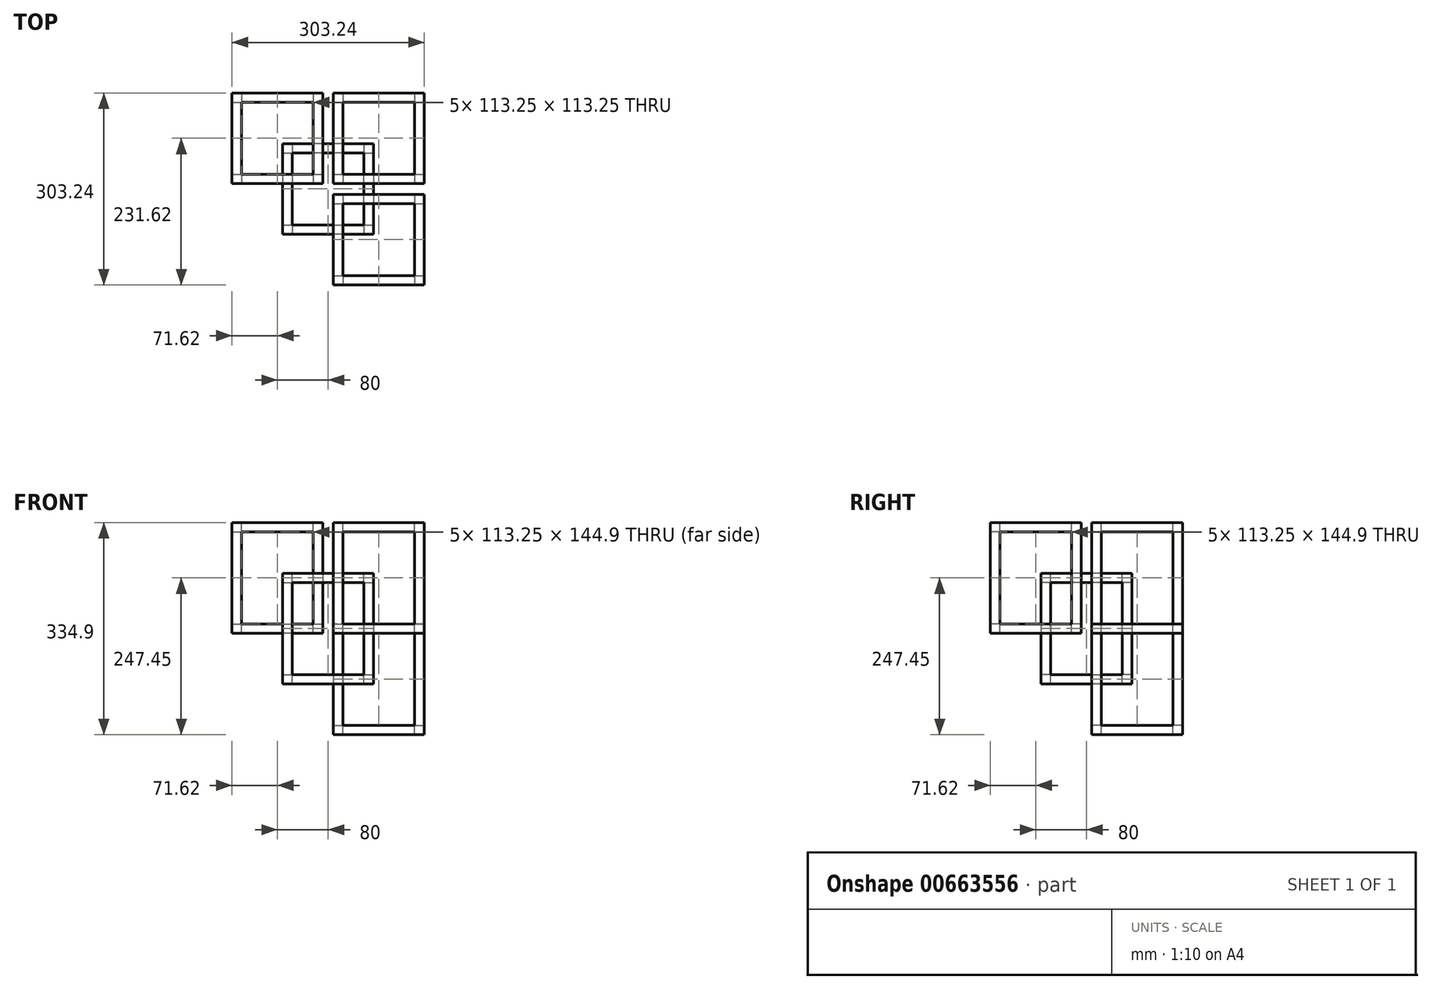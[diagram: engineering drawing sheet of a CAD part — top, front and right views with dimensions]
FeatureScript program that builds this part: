
annotation { "Feature Type Name" : "Feature", "Feature Type Description" : "" }
export const myFeature = defineFeature(function(context is Context, id is Id, definition is map)
    precondition{}
    {
        {
            var Q0;
            Q0=qCreatedBy(makeId("Top.planeOp"),FACE);
            var sketch = newSketch(context, id + "F0", { "sketchPlane" : qUnion([Q0])});
            skLineSegment(sketch, "E0.bottom", {"start": v(71.63, 71.63) * mm, "end": v(-71.62, 71.63) * mm});
            skLineSegment(sketch, "E0.top", {"start": v(71.63, -71.63) * mm, "end": v(-71.62, -71.63) * mm});
            skLineSegment(sketch, "E0.left", {"start": v(71.63, 71.62) * mm, "end": v(71.63, -71.63) * mm});
            skLineSegment(sketch, "E0.right", {"start": v(-71.62, 71.63) * mm, "end": v(-71.62, -71.63) * mm});
            skPoint(sketch, "E0.middle", {"position": v(0, 0) * mm});
            skSolve(sketch);
        }
        {
            var Q0;
            Q0=makeQuery(id+"F0.imprint","IMPRINT",FACE,{"disambiguationData":[TD([[makeQuery(id+"F0.imprint","IMPRINT",EDGE,{"derivedFrom":sQuery(id+"F0.wireOp",EDGE,"E0.bottom")}),1.0]])]});
            extrude(context, id + "F1", {"entities" : qUnion([Q0]), "depth" : 174.9 * mm, "offsetDistance" : 25 * mm});
        }
        {
            var Q0;
            Q0=makeQuery(id+"F1.opExtrude","SWEPT_FACE",FACE,{"disambiguationData":[OSD([sQuery(id+"F0.wireOp",EDGE,"E0.top")])]});
            var sketch = newSketch(context, id + "F2", { "sketchPlane" : qUnion([Q0])});
            skLineSegment(sketch, "E1.0", {"start": v(-56.62, 15) * mm, "end": v(56.63, 15) * mm});
            skLineSegment(sketch, "E1.1", {"start": v(-56.62, 159.9) * mm, "end": v(-56.62, 15) * mm});
            skLineSegment(sketch, "E1.2", {"start": v(56.63, 159.9) * mm, "end": v(-56.62, 159.9) * mm});
            skLineSegment(sketch, "E1.3", {"start": v(56.63, 15) * mm, "end": v(56.63, 159.9) * mm});
            skSolve(sketch);
        }
        {
            var Q0;
            Q0=makeQuery(id+"F2.imprint","IMPRINT",FACE,{"disambiguationData":[TD([[makeQuery(id+"F2.imprint","IMPRINT",EDGE,{"derivedFrom":sQuery(id+"F2.wireOp",EDGE,"E1.0")}),1.0]])]});
            extrude(context, id + "F3", {"entities" : qUnion([Q0]), "operationType" : NewBodyOperationType.REMOVE, "endBound" : BoundingType.THROUGH_ALL, "oppositeDirection" : true, "depth" : 25 * mm, "offsetDistance" : 25 * mm});
        }
        {
            var Q0;
            Q0=makeQuery(id+"F1.opExtrude","SWEPT_FACE",FACE,{"disambiguationData":[OSD([sQuery(id+"F0.wireOp",EDGE,"E0.left")])]});
            var sketch = newSketch(context, id + "F4", { "sketchPlane" : qUnion([Q0])});
            skLineSegment(sketch, "E2.0", {"start": v(-56.63, 15) * mm, "end": v(56.63, 15) * mm});
            skLineSegment(sketch, "E2.1", {"start": v(-56.63, 159.9) * mm, "end": v(-56.63, 15) * mm});
            skLineSegment(sketch, "E2.2", {"start": v(56.63, 159.9) * mm, "end": v(-56.63, 159.9) * mm});
            skLineSegment(sketch, "E2.3", {"start": v(56.63, 15) * mm, "end": v(56.63, 159.9) * mm});
            skSolve(sketch);
        }
        {
            var Q0;
            Q0=makeQuery(id+"F4.imprint","IMPRINT",FACE,{"disambiguationData":[TD([[makeQuery(id+"F4.imprint","IMPRINT",EDGE,{"derivedFrom":sQuery(id+"F4.wireOp",EDGE,"E2.0")}),1.0]])]});
            extrude(context, id + "F5", {"entities" : qUnion([Q0]), "operationType" : NewBodyOperationType.REMOVE, "endBound" : BoundingType.THROUGH_ALL, "oppositeDirection" : true, "depth" : 25 * mm, "offsetDistance" : 25 * mm});
        }
        {
            var Q0;
            Q0=makeQuery(id+"F1.opExtrude","CAP_FACE",FACE,{"disambiguationData":[OSD([sQuery(id+"F0.wireOp",EDGE,"E0.bottom"),sQuery(id+"F0.wireOp",EDGE,"E0.top"),sQuery(id+"F0.wireOp",EDGE,"E0.left"),sQuery(id+"F0.wireOp",EDGE,"E0.right")])],"isStart":false});
            var sketch = newSketch(context, id + "F6", { "sketchPlane" : qUnion([Q0])});
            skLineSegment(sketch, "E3.0", {"start": v(-56.62, -56.63) * mm, "end": v(56.63, -56.63) * mm});
            skLineSegment(sketch, "E3.1", {"start": v(-56.62, 56.62) * mm, "end": v(-56.62, -56.63) * mm});
            skLineSegment(sketch, "E3.2", {"start": v(56.63, 56.63) * mm, "end": v(-56.62, 56.63) * mm});
            skLineSegment(sketch, "E3.3", {"start": v(56.63, -56.63) * mm, "end": v(56.63, 56.63) * mm});
            skSolve(sketch);
        }
        {
            var Q0;
            Q0=makeQuery(id+"F6.imprint","IMPRINT",FACE,{"disambiguationData":[TD([[makeQuery(id+"F6.imprint","IMPRINT",EDGE,{"derivedFrom":sQuery(id+"F6.wireOp",EDGE,"E3.0")}),1.0]])]});
            extrude(context, id + "F7", {"entities" : qUnion([Q0]), "operationType" : NewBodyOperationType.REMOVE, "endBound" : BoundingType.THROUGH_ALL, "oppositeDirection" : true, "depth" : 25 * mm, "offsetDistance" : 25 * mm});
        }
        {
            var Q0;
            Q0=makeQuery(id+"F1.opExtrude","SWEPT_BODY",BODY,{"disambiguationData":[OSD([sQuery(id+"F0.wireOp",EDGE,"E0.bottom"),sQuery(id+"F0.wireOp",EDGE,"E0.top"),sQuery(id+"F0.wireOp",EDGE,"E0.left"),sQuery(id+"F0.wireOp",EDGE,"E0.right")])]});
            transform(context, id + "F8", {"entities" : qUnion([Q0]), "transformType" : TransformType.TRANSLATION_3D, "dx" : 80 * mm, "dy" : 80 * mm, "dz" : 80 * mm, "makeCopy" : true});
        }
        {
            var Q0;
            Q0=makeQuery(id+"F1.opExtrude","SWEPT_BODY",BODY,{"disambiguationData":[OSD([sQuery(id+"F0.wireOp",EDGE,"E0.bottom"),sQuery(id+"F0.wireOp",EDGE,"E0.top"),sQuery(id+"F0.wireOp",EDGE,"E0.left"),sQuery(id+"F0.wireOp",EDGE,"E0.right")])]});
            transform(context, id + "F9", {"entities" : qUnion([Q0]), "transformType" : TransformType.TRANSLATION_3D, "dx" : -80 * mm, "dy" : 80 * mm, "dz" : 80 * mm, "makeCopy" : true});
        }
        {
            var Q0;
            Q0=makeQuery(id+"F1.opExtrude","SWEPT_BODY",BODY,{"disambiguationData":[OSD([sQuery(id+"F0.wireOp",EDGE,"E0.bottom"),sQuery(id+"F0.wireOp",EDGE,"E0.top"),sQuery(id+"F0.wireOp",EDGE,"E0.left"),sQuery(id+"F0.wireOp",EDGE,"E0.right")])]});
            transform(context, id + "F10", {"entities" : qUnion([Q0]), "transformType" : TransformType.TRANSLATION_3D, "dx" : 80 * mm, "dy" : -80 * mm, "dz" : 80 * mm, "makeCopy" : true});
        }
        {
            var Q0;
            Q0=makeQuery(id+"F1.opExtrude","SWEPT_BODY",BODY,{"disambiguationData":[OSD([sQuery(id+"F0.wireOp",EDGE,"E0.bottom"),sQuery(id+"F0.wireOp",EDGE,"E0.top"),sQuery(id+"F0.wireOp",EDGE,"E0.left"),sQuery(id+"F0.wireOp",EDGE,"E0.right")])]});
            transform(context, id + "F11", {"entities" : qUnion([Q0]), "transformType" : TransformType.TRANSLATION_3D, "dx" : 80 * mm, "dy" : 80 * mm, "dz" : -80 * mm, "makeCopy" : true});
        }
    });
